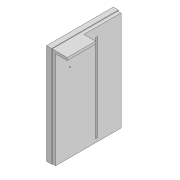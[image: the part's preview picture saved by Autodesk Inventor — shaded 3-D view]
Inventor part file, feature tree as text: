
AUTODESK INVENTOR PART (.ipt)
format: ipt  version: 2022 (Build 260153000, 153)  size: 162,304 bytes
history: native  units: mm
features: reference x18, other x9, extrude x4, sketch x4, hole x1
ambient origin geometry x8: Origin, YZ Plane, XZ Plane, XY Plane, X Axis, Y Axis, Z Axis, Center Point
bodies: Body1 (feature_tree)
feature tree (36):
  other  "Твердое тело1"
  extrude  "Выдавливание1"  Depth=400.0mm
  extrude  "Выдавливание3"  Depth=600.0mm
  extrude  "Выдавливание4"  Depth=50.0mm TaperAngle=0.0deg
  hole  "Отверстие1"  [1 undecoded]
  extrude  "Выдавливание5"  Depth=4.0mm
  sketch  "Эскиз3"
  sketch  "Эскиз4"
  reference  "Ссылка1"
  reference  "Ссылка2"
  reference  "Ссылка3"
  reference  "Ссылка4"
  reference  "Ссылка5"
  reference  "Ссылка6"
  reference  "Ссылка7"
  reference  "Ссылка8"
  reference  "Ссылка9"
  reference  "Ссылка10"
  reference  "Ссылка11"
  reference  "Ссылка12"
  reference  "Ссылка13"
  reference  "Ссылка14"
  reference  "Ссылка15"
  reference  "Ссылка16"
  reference  "Ссылка17"
  sketch  "Эскиз5"
  reference  "Ссылка18"
  sketch  "Эскиз6"
  other  "<userpath>\Documents\Inventor\Файлы Inventor\Сборка всего.iam"
  other  "Сборка всего.iam"
  other  "Конвейр сборка:1"
  other  "Конвейр без шпилек сборка:1"
  other  "Подставка для двигателя и драйвера:3"
  other  "Подставка для двигателя и драйвера:2"
  other  "Барабан сборка:1"
  other  "Стенка барабана:1"
note: 1 required parameter value undecoded (feature->parameter linkage not recoverable at this tier; creation-order binding heuristic only, values carry confidence <= 0.55)
